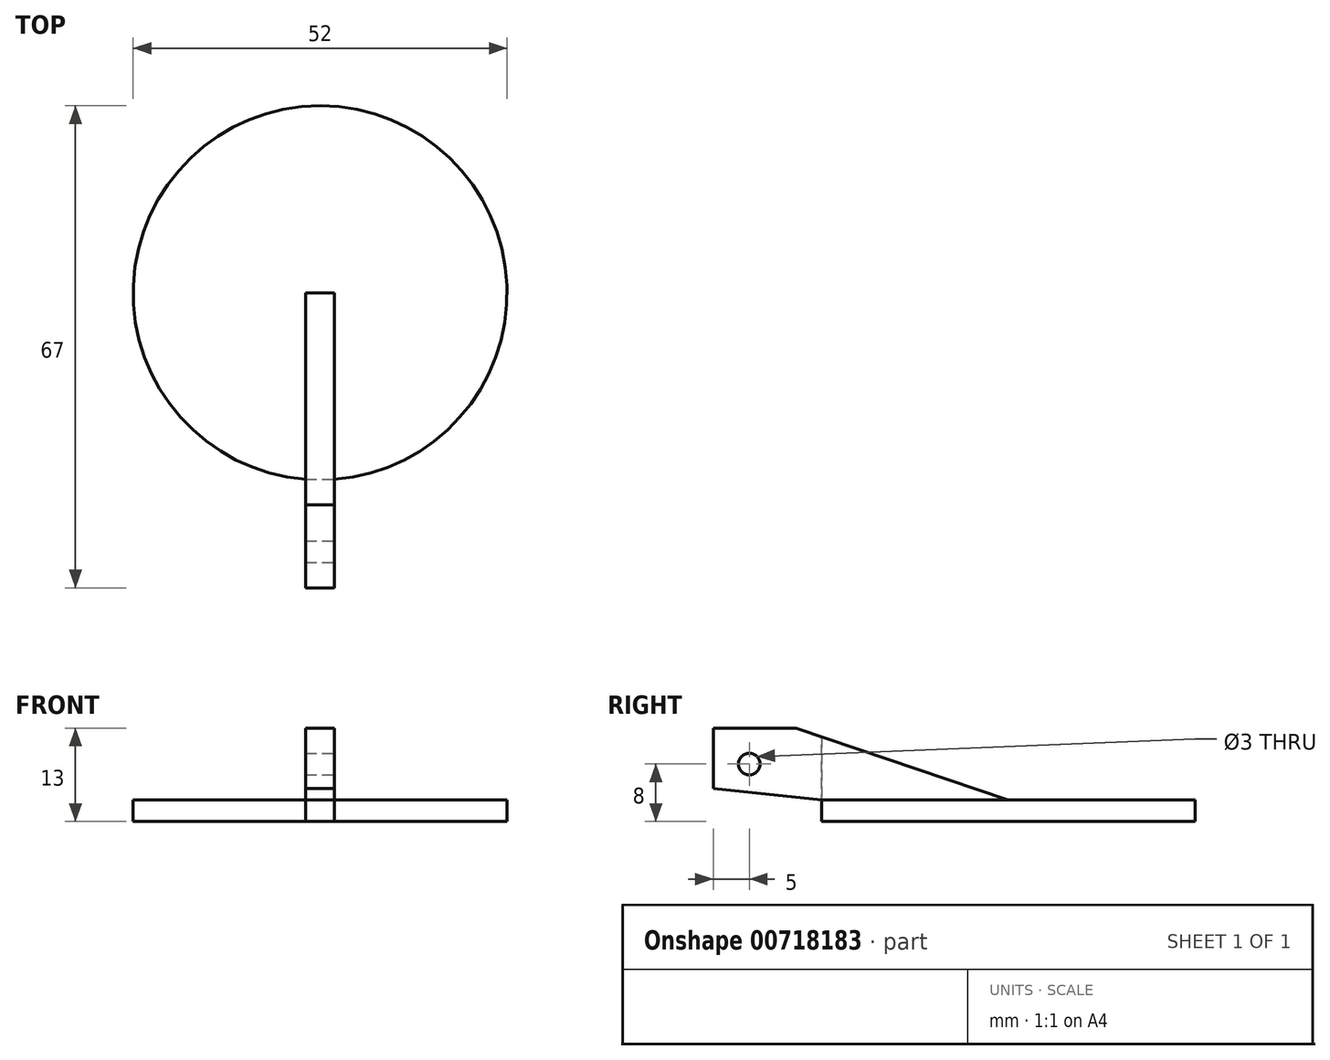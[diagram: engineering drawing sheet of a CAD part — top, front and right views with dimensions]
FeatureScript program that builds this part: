
annotation { "Feature Type Name" : "Feature", "Feature Type Description" : "" }
export const myFeature = defineFeature(function(context is Context, id is Id, definition is map)
    precondition{}
    {
        {
            var Q0;
            Q0=qCreatedBy(makeId("Top.planeOp"),FACE);
            var sketch = newSketch(context, id + "F0", { "sketchPlane" : qUnion([Q0])});
            skArc(sketch, "E0", {"start": v(2, -25.92) * mm, "mid": v(0, 26) * mm, "end": v(-2, -25.92) * mm});
            skLineSegment(sketch, "E1.top", {"start": v(-2, -41) * mm, "end": v(2, -41) * mm});
            skLineSegment(sketch, "E1.left", {"start": v(-2, -25.92) * mm, "end": v(-2, -41) * mm});
            skLineSegment(sketch, "E1.right", {"start": v(2, -25.92) * mm, "end": v(2, -41) * mm});
            skPoint(sketch, "E1.bottom.start.orphan", {"position": v(-2, 0) * mm});
            skSolve(sketch);
        }
        {
            var Q0;
            Q0=makeQuery(id+"F0.imprint","IMPRINT",FACE,{"disambiguationData":[TD([[makeQuery(id+"F0.imprint","IMPRINT",EDGE,{"derivedFrom":sQuery(id+"F0.wireOp",EDGE,"E0")}),1.0]])]});
            extrude(context, id + "F1", {"entities" : qUnion([Q0]), "oppositeDirection" : true, "depth" : 3 * mm, "offsetDistance" : 25 * mm});
        }
        {
            var Q0;
            Q0=makeQuery(id+"F1.opExtrude","CAP_FACE",FACE,{"disambiguationData":[OSD([sQuery(id+"F0.wireOp",EDGE,"E0"),sQuery(id+"F0.wireOp",EDGE,"E1.top"),sQuery(id+"F0.wireOp",EDGE,"E1.left"),sQuery(id+"F0.wireOp",EDGE,"E1.right")])],"isStart":true});
            var sketch = newSketch(context, id + "F2", { "sketchPlane" : qUnion([Q0])});
            skLineSegment(sketch, "E2.bottom", {"start": v(-2.02, 0) * mm, "end": v(2, 0) * mm});
            skLineSegment(sketch, "E2.top", {"start": v(-2.02, -41) * mm, "end": v(2, -41) * mm});
            skLineSegment(sketch, "E2.left", {"start": v(-2.02, 0) * mm, "end": v(-2.02, -41) * mm});
            skLineSegment(sketch, "E2.right", {"start": v(2, 0) * mm, "end": v(2, -41) * mm});
            skSolve(sketch);
        }
        {
            var Q0;
            {var subQ1=sQuery(id+"F2.wireOp",EDGE,"E2.bottom");Q0=makeQuery(id+"F2.imprint","IMPRINT",FACE,{"disambiguationData":[TD([[makeQuery(id+"F2.imprint","IMPRINT",EDGE,{"derivedFrom":subQ1}),-1.0]])]});}
            extrude(context, id + "F3", {"entities" : qUnion([Q0]), "operationType" : NewBodyOperationType.ADD, "depth" : 10 * mm, "offsetDistance" : 25 * mm});
        }
        {
            var Q0;
            Q0=makeQuery(id+"F3.boolean.opBoolean","MERGE",FACE,{"derivedFrom":[makeQuery(id+"F1.opExtrude","SWEPT_FACE",FACE,{"disambiguationData":[OSD([sQuery(id+"F0.wireOp",EDGE,"E1.right")])]}),makeQuery(id+"F3.opExtrude","SWEPT_FACE",FACE,{"disambiguationData":[OSD([sQuery(id+"F2.wireOp",EDGE,"E2.right")])]})]});
            var sketch = newSketch(context, id + "F4", { "sketchPlane" : qUnion([Q0])});
            skLineSegment(sketch, "E3", {"start": v(0, 0) * mm, "end": v(-29.48, 10) * mm});
            skSolve(sketch);
        }
        {
            var Q0;
            {var subQ0=sQuery(id+"F4.wireOp",EDGE,"E3");Q0=makeQuery(id+"F4.imprint","IMPRINT",FACE,{"disambiguationData":[TD([[makeQuery(id+"F4.imprint","IMPRINT",EDGE,{"derivedFrom":subQ0}),-1.0]])]});}
            extrude(context, id + "F5", {"entities" : qUnion([Q0]), "operationType" : NewBodyOperationType.REMOVE, "oppositeDirection" : true, "depth" : 25 * mm, "offsetDistance" : 25 * mm});
        }
        {
            var Q0;
            Q0=makeQuery(id+"F1.opExtrude","CAP_FACE",FACE,{"disambiguationData":[OSD([sQuery(id+"F0.wireOp",EDGE,"E0"),sQuery(id+"F0.wireOp",EDGE,"E1.top"),sQuery(id+"F0.wireOp",EDGE,"E1.left"),sQuery(id+"F0.wireOp",EDGE,"E1.right")])],"isStart":false});
            var sketch = newSketch(context, id + "F6", { "sketchPlane" : qUnion([Q0])});
            skLineSegment(sketch, "E4.bottom", {"start": v(-2.28, 41) * mm, "end": v(2.18, 41) * mm});
            skLineSegment(sketch, "E4.top", {"start": v(-2.28, 25.96) * mm, "end": v(2.18, 25.96) * mm});
            skLineSegment(sketch, "E4.left", {"start": v(-2.28, 41) * mm, "end": v(-2.28, 25.96) * mm});
            skLineSegment(sketch, "E4.right", {"start": v(2.18, 41) * mm, "end": v(2.18, 25.96) * mm});
            skSolve(sketch);
        }
        {
            var Q0;
            Q0 = qSketchRegion(id + "F6", true);
            var Q1;
            {var subQ0=sQuery(id+"F6.wireOp",EDGE,"E4.bottom");var subQ1=makeQuery(id+"F1.opExtrude","CAP_EDGE",EDGE,{"disambiguationData":[OSD([sQuery(id+"F0.wireOp",EDGE,"E1.left")])],"isStart":false});var subQ2=makeQuery(id+"F6.imprint","INTERSECT",VERTEX,{"derivedFrom":[subQ1,subQ0]});Q1=makeQuery(id+"F6.imprint","IMPRINT",FACE,{"disambiguationData":[TD([[makeQuery(id+"F6.imprint","IMPRINT",EDGE,{"disambiguationData":[TD([[subQ2,-1.0]])],"derivedFrom":subQ0}),-1.0]])]});}
            extrude(context, id + "F7", {"entities" : qUnion([Q0, Q1]), "operationType" : NewBodyOperationType.REMOVE, "oppositeDirection" : true, "depth" : 3 * mm, "offsetDistance" : 25 * mm});
        }
        {
            var Q0;
            Q0=makeQuery(id+"F3.boolean.opBoolean","MERGE",FACE,{"derivedFrom":[makeQuery(id+"F1.opExtrude","SWEPT_FACE",FACE,{"disambiguationData":[OSD([sQuery(id+"F0.wireOp",EDGE,"E1.right")])]}),makeQuery(id+"F3.opExtrude","SWEPT_FACE",FACE,{"disambiguationData":[OSD([sQuery(id+"F2.wireOp",EDGE,"E2.right")])]})]});
            var sketch = newSketch(context, id + "F8", { "sketchPlane" : qUnion([Q0])});
            skCircle(sketch, "E5", {"center": v(-36, 5) * mm, "radius": 1.5 * mm});
            skSolve(sketch);
        }
        {
            var Q0;
            Q0=makeQuery(id+"F8.imprint","IMPRINT",FACE,{"disambiguationData":[TD([[makeQuery(id+"F8.imprint","IMPRINT",EDGE,{"derivedFrom":sQuery(id+"F8.wireOp",EDGE,"E5")}),1.0]])]});
            var Q1;
            Q1=sQuery(id+"F8.wireOp",EDGE,"E5");
            extrude(context, id + "F9", {"entities" : qUnion([Q0]), "operationType" : NewBodyOperationType.REMOVE, "surfaceEntities" : qUnion([Q1]), "oppositeDirection" : true, "depth" : 25 * mm, "offsetDistance" : 25 * mm});
        }
        {
            var Q0;
            Q0=makeQuery(id+"F3.boolean.opBoolean","MERGE",FACE,{"derivedFrom":[makeQuery(id+"F1.opExtrude","SWEPT_FACE",FACE,{"disambiguationData":[OSD([sQuery(id+"F0.wireOp",EDGE,"E1.right")])]}),makeQuery(id+"F3.opExtrude","SWEPT_FACE",FACE,{"disambiguationData":[OSD([sQuery(id+"F2.wireOp",EDGE,"E2.right")])]})]});
            var sketch = newSketch(context, id + "F10", { "sketchPlane" : qUnion([Q0])});
            skLineSegment(sketch, "E6", {"start": v(-25.92, 0) * mm, "end": v(-41, 1.57) * mm});
            skSolve(sketch);
        }
        {
            var Q0;
            {var subQ5=sQuery(id+"F10.wireOp",EDGE,"E6");Q0=makeQuery(id+"F10.imprint","IMPRINT",FACE,{"disambiguationData":[TD([[makeQuery(id+"F10.imprint","IMPRINT",EDGE,{"derivedFrom":subQ5}),1.0]])]});}
            extrude(context, id + "F11", {"entities" : qUnion([Q0]), "operationType" : NewBodyOperationType.REMOVE, "oppositeDirection" : true, "depth" : 25 * mm, "offsetDistance" : 25 * mm});
        }
    });
